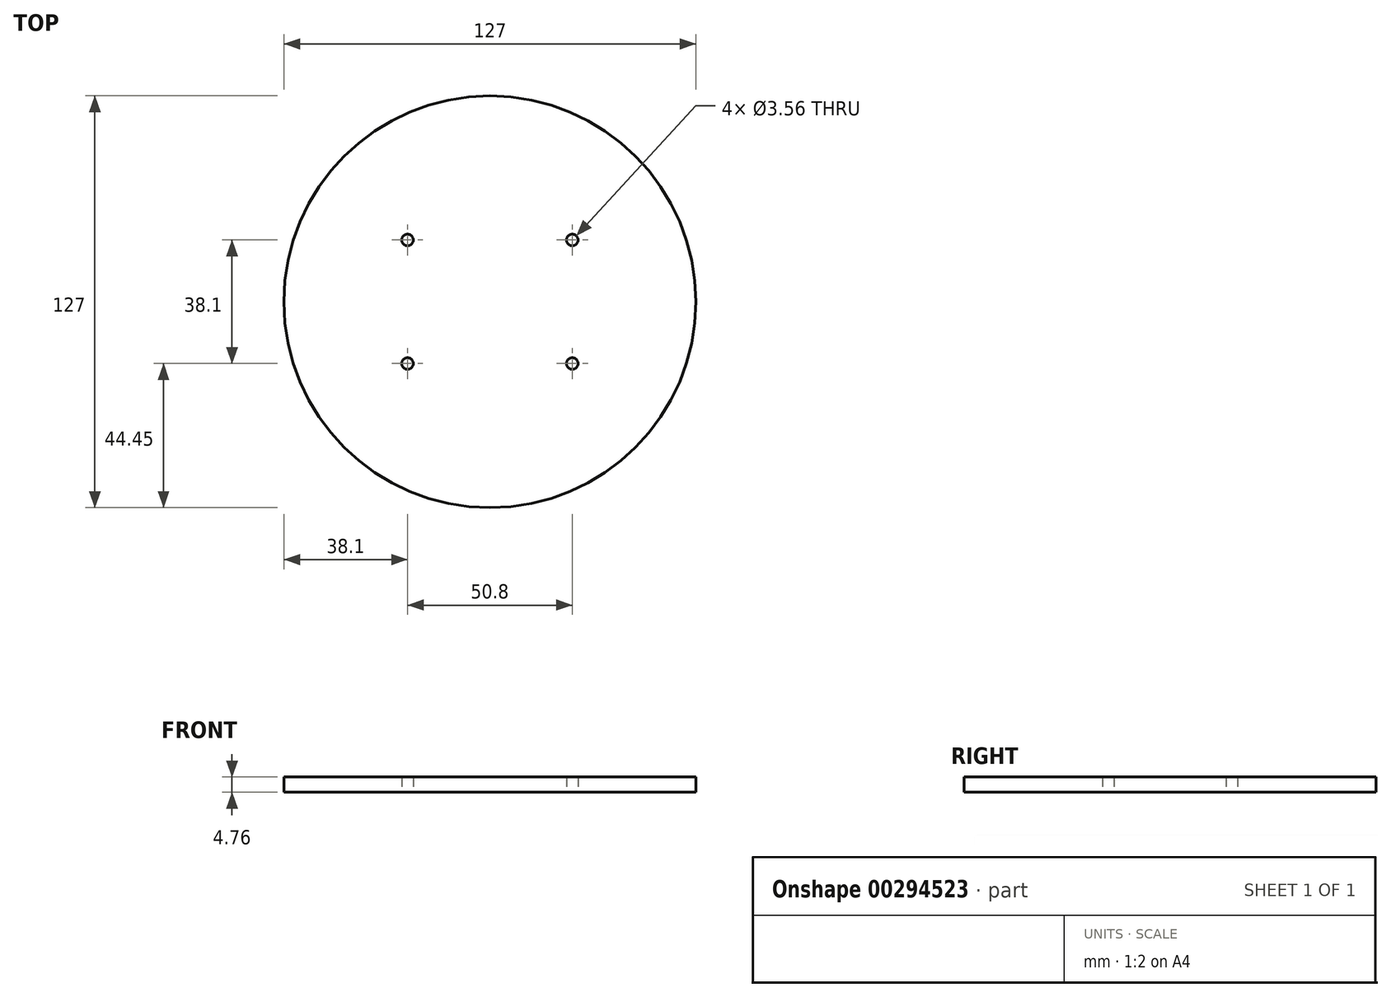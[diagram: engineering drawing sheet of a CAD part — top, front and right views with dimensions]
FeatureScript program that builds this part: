
annotation { "Feature Type Name" : "Feature", "Feature Type Description" : "" }
export const myFeature = defineFeature(function(context is Context, id is Id, definition is map)
    precondition{}
    {
        {
            var Q0;
            Q0=qCreatedBy(makeId("Top.planeOp"),FACE);
            var sketch = newSketch(context, id + "F0", { "sketchPlane" : qUnion([Q0])});
            skCircle(sketch, "E0", {"center": v(0, 0) * mm, "radius": 63.5 * mm});
            skLineSegment(sketch, "E1", {"start": v(0, 0) * mm, "end": v(63.5, 0) * mm, "construction": true});
            skLineSegment(sketch, "E2", {"start": v(25.4, 0) * mm, "end": v(25.4, 19.05) * mm, "construction": true});
            skCircle(sketch, "E3", {"center": v(25.4, 19.05) * mm, "radius": 1.78 * mm});
            skCircle(sketch, "E4.MirrorC", {"center": v(25.4, -19.05) * mm, "radius": 1.78 * mm});
            skLineSegment(sketch, "E5", {"start": v(0, 0) * mm, "end": v(0, -33.46) * mm, "construction": true});
            skCircle(sketch, "E6.MirrorC", {"center": v(-25.4, 19.05) * mm, "radius": 1.78 * mm});
            skCircle(sketch, "E7.MirrorC", {"center": v(-25.4, -19.05) * mm, "radius": 1.78 * mm});
            skSolve(sketch);
        }
        {
            var Q0;
            Q0=makeQuery(id+"F0.imprint","IMPRINT",FACE,{"disambiguationData":[TD([[makeQuery(id+"F0.imprint","IMPRINT",EDGE,{"derivedFrom":sQuery(id+"F0.wireOp",EDGE,"E0")}),1.0]])]});
            extrude(context, id + "F1", {"entities" : qUnion([Q0]), "depth" : 4.76 * mm});
        }
    });
